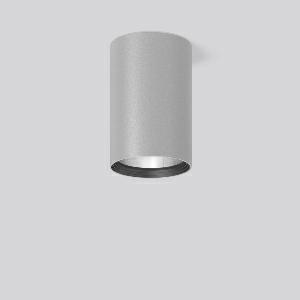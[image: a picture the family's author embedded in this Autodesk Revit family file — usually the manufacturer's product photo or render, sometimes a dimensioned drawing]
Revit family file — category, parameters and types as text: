
# Revit family: heledon_maxi_a_931216_004_2_866e
name_source: partatom
category: Lighting Fixtures
units: mm (PartAtom-declared; Revit-internal decimal feet)

## family parameters
Cut with Voids When Loaded = No
Host = Face
Light Source = No
Part Type = Normal
Room Calculation Point = No
Round Connector Dimension = Use Diameter
Shared = No

## types (1)
- HELEDON maxi A (1 x LED Modul 927, 3050 lm, 2700)
    Apparent Load = 25 VA
    Approval mark = CE
    CIE Flux Codes = 100 100 100 100 100
    Color Rendering = 92
    Color Temperature = 2700
    Default Elevation = 1800 mm
    Description = Series: HELEDON maxi
Cylindrical surface-mounted downlight. Housing: die-cast aluminium, powder-coated. Internal ceiling frame polycarbonate with bayonet mounting. Black plastic ring and recessed LED to prevent glare from the side. Optical assembly with reflector made of MIRO-Silver with 98% total light reflection for outstanding efficiency - can be changed without tools. Best colour rendering index Ra>90. Suitable for Ceiling mounting. Easy installation with a separate ceiling frame with bayonet mounting and plug connection. Driver integrated. Connected via plug-in connector. High quality converter without flickering and stroboscopic effect. The following accessories can be mounted without use of tools: interchangeable lenses, decorative glasses, honeycomb louvre, clear and frosted diffusers, white interchangeable plastic ring. 
Colour: silver
Diameter: 123 mm
Height: 183 mm
Lamp: LED
Socket: without socket
Colour temperature: 2700K
Colour rendering index (CRI): 92
System power: 25 W
Rated luminous flux: 3050 lm
Luminous efficiency: 122 lm/W
Control gear: Regulated power supply
Protection class: I
Type of protection: IP 20
    Height = 183 mm
    Lamp = 1 x LED Modul 927
    Lamp Light Flux = 3050 lm
    Lamp count = 1
    Length = 123 mm
    Lifetime = 50000 h
    Luminous efficacy = 122 lm/W
    Manufacturer = RZB
    ModVariant = No
    Model = 931216.004.2
    Mounting Place = Ceiling
    Mounting Type = Surface mounted
    Number of Poles = 1
    OnlyDefault = Yes
    Power Factor = 1
    Product Name = HELEDON maxi A
    Product group = Surface mounted downlights
    ProductGroupID = 302
    Protection Class = Protection class I
    Protection Degree = IP 20
    RLX_Detail_Level = 1
    RLX_Emergency_Light_Flux = 0 lm
    RLX_Emergency_Type = 0
    RLX_Emergency_Type_DB = No
    RlxData = <blob elided: 98045 chars, md5=3d4fdff0>
    Socket = socket
    Standby Power = 0 W
    System Light Flux = 3050 lm
    System Power = 25 W
    Type Comments = Product without accessories
    Type Image = 931192.004.jpg
    URL = http://relux.com
    VarID = ---
    Voltage = 230 V
    Voltage Range = 220-240 V
    Weight = 0.00 kg
    Width = 0 mm  [stored 0 ft]

note: [stored X ft] marks values corroborated as IEEE doubles in the binary element streams (Revit-internal decimal feet)

## geometry (parser evidence)
native form markers: Blend x4, Sweep x11
no freeform markers — native parametric forms only
